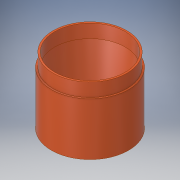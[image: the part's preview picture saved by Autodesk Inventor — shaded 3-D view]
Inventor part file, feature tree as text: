
AUTODESK INVENTOR PART (.ipt)
format: ipt  version: 2017 SP1 (Build 210196100, 196)  size: 162,304 bytes
history: native  units: in
note: dims shown in document units (in); Inventor stores cm internally (conversion verified against a paired STEP export)
features: revolve x1, sketch x1
ambient origin geometry x8: Origin, YZ Plane, XZ Plane, XY Plane, X Axis, Y Axis, Z Axis, Center Point
bodies: Solid1 (feature_tree)
feature tree (2):
  revolve  "Revolution1"  [1 undecoded]
  sketch  "Sketch1"  dims[d0=0.5in d1=1.13in d3=15.0deg d4=0.25in d9=1.5in d11=0.5in d13=3.75in d14=0.25in d15=1.0in d16=0.25in d17=0.5in d18=0.234in d19=0.234in d20=0.5in d22=4.25in d23=2.5in d25=1.0in d26=0.25in d27=5.25in d28=0.125in d29=4.0in d30=0.25in d31=0.1718in d32=1.75in d33=0.125in d34=0.801in d35=0.375in d37=90.0deg]
note: 1 required parameter value undecoded (feature->parameter linkage not recoverable at this tier; creation-order binding heuristic only, values carry confidence <= 0.55)
